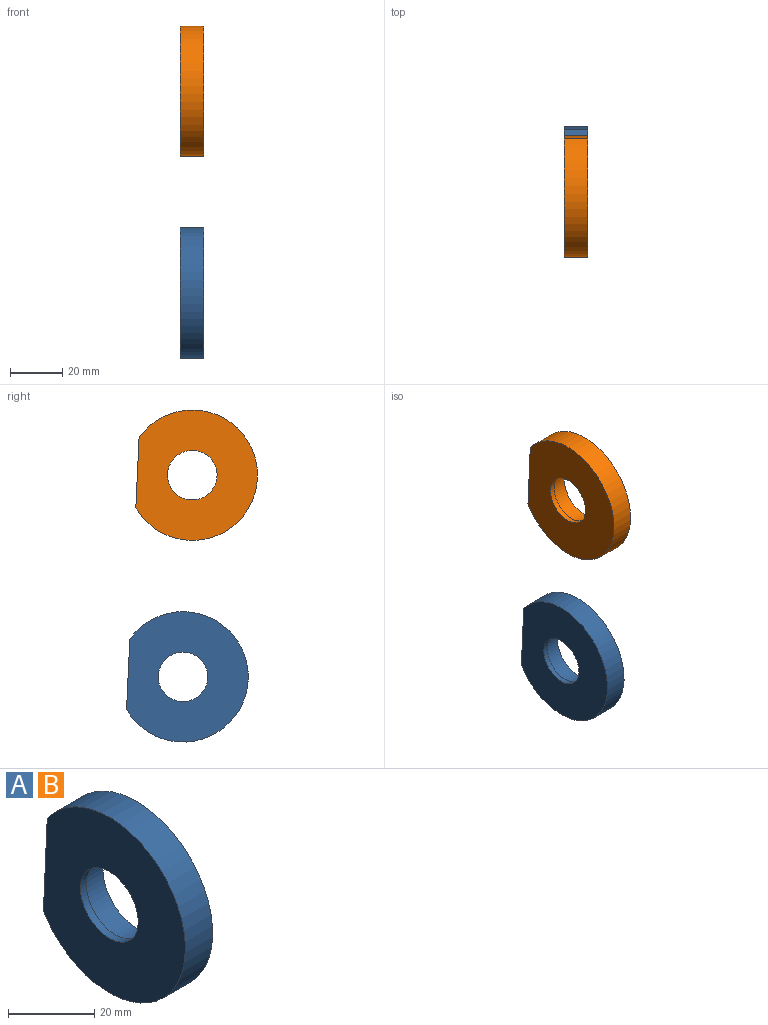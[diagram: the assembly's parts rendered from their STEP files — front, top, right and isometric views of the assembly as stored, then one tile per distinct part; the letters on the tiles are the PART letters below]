
ASSEMBLY  parts=2 mates=2
PART A: 7 faces, bbox 9x46.6x50 mm
  f0: plane 22.15x22.15mm, normal (1,0,0), area 101.8mm2, adj f2,f5
  f1: plane 26.97x9mm, normal (0,1,0.05), area 243mm2, adj f3,f4,f6
  f2: cylinder r=9.5mm len=19mm, axis (1,0,0), area 119.4mm2, adj f0,f4
  f3: cylinder r=25mm len=50mm, axis (1,0,0), area 1157mm2, adj f1,f4,f6
  f4: plane 50x46.64mm, normal (-1,0,0), area 1607.5mm2, adj f1,f2,f3
  f5: cylinder r=11.07mm len=22.15mm, axis (-1,0,0), area 487.1mm2, adj f0,f6
  f6: plane 50x46.64mm, normal (1,0,0), area 1505.7mm2, adj f1,f3,f5
PART B: same geometry as A
PLACE A t=(-63.53,43.28,-85.03)mm
PLACE B t=(-63.53,39.72,-7.74)mm
MATE planar B.f6 <-> A.f6  axis (1,0,0) through (-56.53,38.63,-7.79)mm
MATE planar A.f1 <-> B.f1  axis (0,1,0.05) through (-61.03,64.3,-84.06)mm
